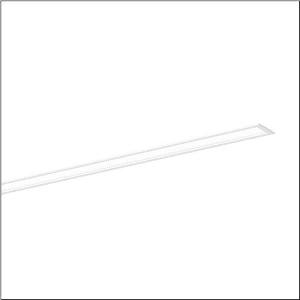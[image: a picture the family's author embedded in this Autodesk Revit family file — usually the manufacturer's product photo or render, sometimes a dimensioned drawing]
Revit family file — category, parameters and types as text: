
# Revit family: silica_r__21_51mx13tat4w_7811
name_source: partatom
category: Lighting Fixtures
units: mm (PartAtom-declared; Revit-internal decimal feet)

## family parameters
Cut with Voids When Loaded = No
Host = Face
Light Source = No
Part Type = Normal
Room Calculation Point = No
Round Connector Dimension = Use Diameter
Shared = No

## types (1)
- --- (1 x LED, 3230 lm, 32.4 W, 6500K)
    Apparent Load = 32 VA
    CIE Flux Codes = 78 96 99 100 100
    Color Rendering = 80
    Color Temperature = 6500K
    Default Elevation = 1800 mm
    Description = Silica® 21, office luminaire, primary optical cover: prismatic diffuser, of PMMA, CAT 2 (L<= 3000cd/m²), light emission: direct distribution, primary light characteristic: symmetric, installation type: recessed, LED, rated luminous flux: 3.230lm, luminous efficacy: 95lm/W, light colour: 8tw, colour temperature: 2700..6500K, with terminal, 3+2-pole, max. 2.5mm², mains connection: 220..240V, AC, 50/60Hz, rated input power: 34W, luminaire housing, of aluminium, traffic white (RAL 9016), length: 1.228mm, width: 79mm, height: 53mm, protection rating (complete): IP20, insulation class (complete): insulation class I (protective earthing), certification: CE, permissible operating ambient temperature: 0..+35°C, standard: EN 50419, packaging unit: 1 piece
    Height = 0 mm  [stored 0 ft]
    Lamp = 1 x LED
    Lamp Light Flux = 3230 lm
    Lamp Power = 32.4 W
    Lamp count = 1
    Length = 1227 mm
    Luminous efficacy = 100 lm/W
    Manufacturer = Siteco
    ModVariant = No
    Model = 51MX13TAT4W
    Mounting Place = Ceiling
    Mounting Type = Recessed
    Number of Poles = 1
    OnlyDefault = Yes
    Power Factor = 1
    Product Name = Silica® 21
    Product group = office luminaire | ceiling recessed
    ProductGroupID = 401
    Protection Class = Protection class I
    Protection Degree = IP 20
    RLX_Detail_Level = 1
    RLX_Emergency_Light_Flux = 0 lm
    RLX_Emergency_Type = 0
    RLX_Emergency_Type_DB = No
    RlxData = <blob elided: 13065 chars, md5=fdf53f7d>
    Socket = socket
    Standby Power = 0 W
    System Light Flux = 3230 lm
    System Power = 32 W
    Type Comments = individual setting
    Type Image = l_1313611.jpg
    URL = http://relux.com
    VarID = @adj_089223
    Voltage = 0 V
    Weight = 0.00 kg
    Width = 79 mm

note: [stored X ft] marks values corroborated as IEEE doubles in the binary element streams (Revit-internal decimal feet)

## geometry (parser evidence)
native form markers: Sweep x9
no freeform markers — native parametric forms only
